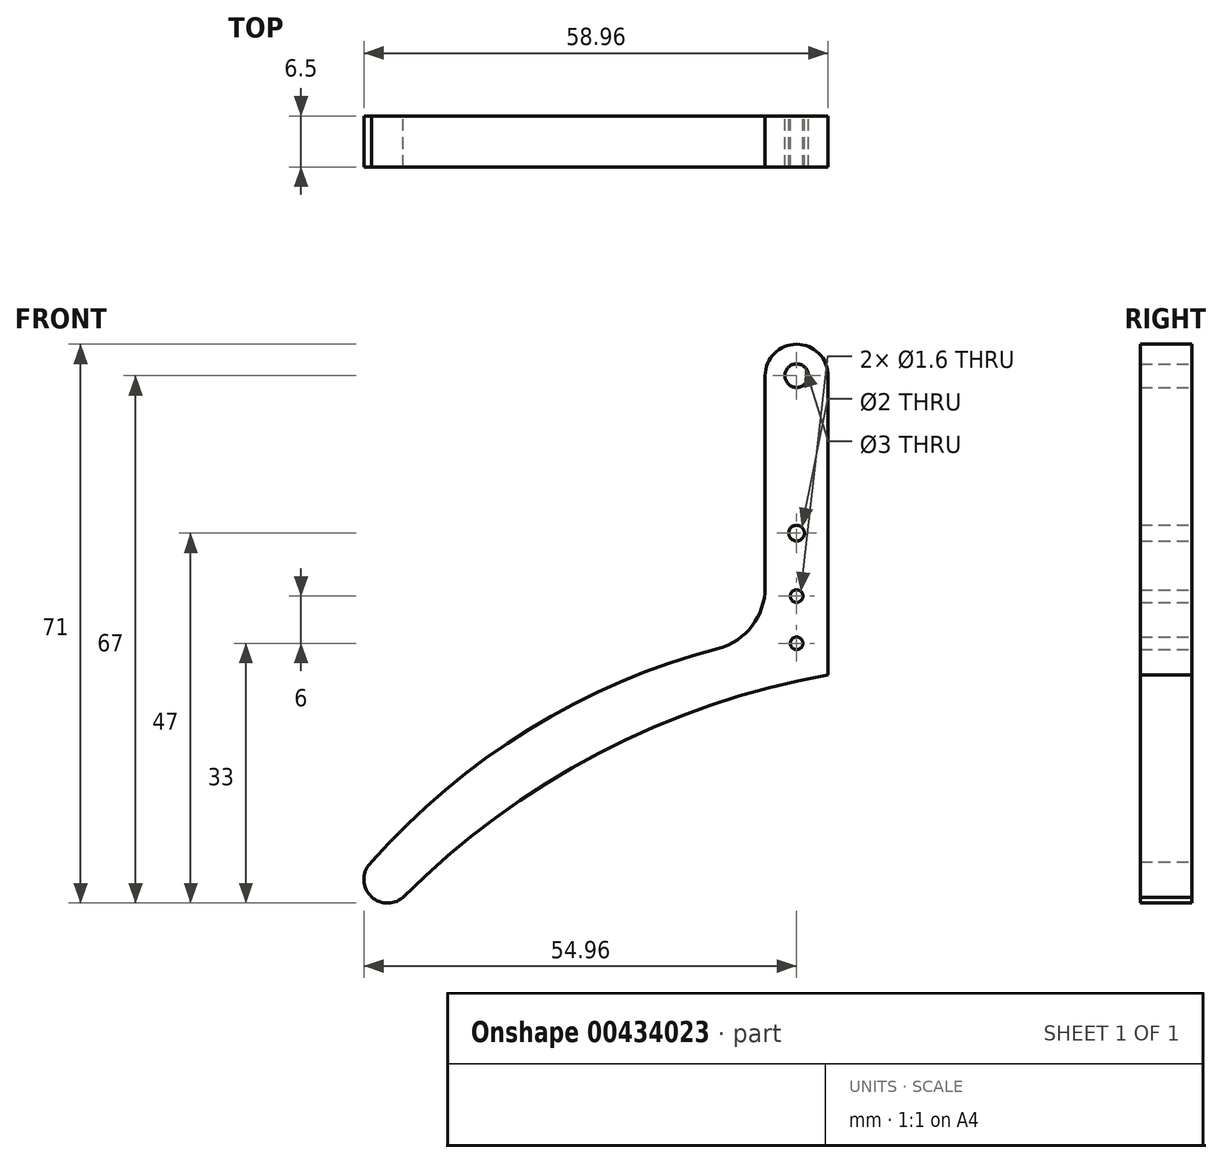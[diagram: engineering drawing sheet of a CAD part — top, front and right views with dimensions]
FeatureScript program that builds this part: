
annotation { "Feature Type Name" : "Feature", "Feature Type Description" : "" }
export const myFeature = defineFeature(function(context is Context, id is Id, definition is map)
    precondition{}
    {
        {
            var Q0;
            Q0=qCreatedBy(makeId("Front.planeOp"),FACE);
            var sketch = newSketch(context, id + "F0", { "sketchPlane" : qUnion([Q0])});
            skCircle(sketch, "E0", {"center": v(0, 34) * mm, "radius": 4 * mm});
            skCircle(sketch, "E1", {"center": v(0, 0) * mm, "radius": 4 * mm});
            skCircle(sketch, "E2", {"center": v(0, 34) * mm, "radius": 1.5 * mm});
            skCircle(sketch, "E3", {"center": v(-51.96, -30) * mm, "radius": 3 * mm});
            skLineSegment(sketch, "E4", {"start": v(-4, 34) * mm, "end": v(-4, 7.1) * mm});
            skLineSegment(sketch, "E5", {"start": v(4, 34) * mm, "end": v(4, 0) * mm});
            skCircle(sketch, "E6", {"center": v(0, 14) * mm, "radius": 1 * mm});
            skLineSegment(sketch, "E7.bottom", {"start": v(4, 0) * mm, "end": v(0, 0) * mm});
            skLineSegment(sketch, "E7.top", {"start": v(4, -4) * mm, "end": v(0, -4) * mm});
            skLineSegment(sketch, "E7.left", {"start": v(4, 0) * mm, "end": v(4, -4) * mm});
            skLineSegment(sketch, "E7.right", {"start": v(0, 0) * mm, "end": v(0, -4) * mm});
            skLineSegment(sketch, "E8.left", {"start": v(0, 0) * mm, "end": v(0, 34) * mm});
            skLineSegment(sketch, "E9", {"start": v(0, 0) * mm, "end": v(-51.96, -30) * mm, "construction": true});
            skPoint(sketch, "E10.visualSharp", {"position": v(-4, 0) * mm});
            skArc(sketch, "E11.filletArc", {"start": v(-9.94, -0.64) * mm, "mid": v(-5.66, 2.22) * mm, "end": v(-4, 7.1) * mm});
            skCircle(sketch, "E12", {"center": v(0, 6) * mm, "radius": 0.8 * mm});
            skCircle(sketch, "E13", {"center": v(0, 0) * mm, "radius": 0.8 * mm});
            skArc(sketch, "E14", {"start": v(-9.94, -0.64) * mm, "mid": v(-33.99, -10.93) * mm, "end": v(-54, -27.8) * mm});
            skArc(sketch, "E15", {"start": v(4, -4) * mm, "mid": v(-25.18, -14) * mm, "end": v(-50.02, -32.28) * mm});
            skSolve(sketch);
        }
        {
            var Q0;
            Q0=makeQuery(id+"F0.imprint","IMPRINT",FACE,{"disambiguationData":[TD([[makeQuery(id+"F0.imprint","IMPRINT",EDGE,{"derivedFrom":sQuery(id+"F0.wireOp",EDGE,"E2")}),-1.0]])]});
            var Q1;
            {var subQ0=sQuery(id+"F0.wireOp",EDGE,"E5");Q1=makeQuery(id+"F0.imprint","IMPRINT",FACE,{"disambiguationData":[TD([[makeQuery(id+"F0.imprint","IMPRINT",EDGE,{"derivedFrom":subQ0}),-1.0]])]});}
            var Q2;
            {var subQ5=sQuery(id+"F0.wireOp",EDGE,"E4");Q2=makeQuery(id+"F0.imprint","IMPRINT",FACE,{"disambiguationData":[TD([[makeQuery(id+"F0.imprint","IMPRINT",EDGE,{"derivedFrom":subQ5}),1.0]])]});}
            var Q3;
            {var subQ0=sQuery(id+"F0.wireOp",EDGE,"E7.bottom");var subQ5=sQuery(id+"F0.wireOp",EDGE,"E13");var subQ6=makeQuery(id+"F0.imprint","INTERSECT",VERTEX,{"derivedFrom":[subQ0,subQ5]});Q3=makeQuery(id+"F0.imprint","IMPRINT",FACE,{"disambiguationData":[TD([[makeQuery(id+"F0.imprint","IMPRINT",EDGE,{"disambiguationData":[TD([[subQ6,1.0]])],"derivedFrom":subQ5}),-1.0]])]});}
            var Q4;
            {var subQ2=sQuery(id+"F0.wireOp",EDGE,"E7.top");Q4=makeQuery(id+"F0.imprint","IMPRINT",FACE,{"disambiguationData":[TD([[makeQuery(id+"F0.imprint","IMPRINT",EDGE,{"derivedFrom":subQ2}),-1.0]])]});}
            var Q5;
            {var subQ1=sQuery(id+"F0.wireOp",EDGE,"E1");var subQ3=sQuery(id+"F0.wireOp",EDGE,"E8.left");var subQ4=makeQuery(id+"F0.imprint","INTERSECT",VERTEX,{"derivedFrom":[subQ1,subQ3]});Q5=makeQuery(id+"F0.imprint","IMPRINT",FACE,{"disambiguationData":[TD([[makeQuery(id+"F0.imprint","IMPRINT",EDGE,{"disambiguationData":[TD([[subQ4,1.0]])],"derivedFrom":subQ3}),1.0]])]});}
            var Q6;
            {var subQ1=sQuery(id+"F0.wireOp",EDGE,"E1");var subQ3=sQuery(id+"F0.wireOp",EDGE,"E8.left");var subQ4=makeQuery(id+"F0.imprint","INTERSECT",VERTEX,{"derivedFrom":[subQ1,subQ3]});Q6=makeQuery(id+"F0.imprint","IMPRINT",FACE,{"disambiguationData":[TD([[makeQuery(id+"F0.imprint","IMPRINT",EDGE,{"disambiguationData":[TD([[subQ4,1.0]])],"derivedFrom":subQ3}),-1.0]])]});}
            var Q7;
            {var subQ0=sQuery(id+"F0.wireOp",EDGE,"E3");var subQ1=makeQuery(id+"F0.imprint","INTERSECT",VERTEX,{"derivedFrom":[subQ0,sQuery(id+"F0.wireOp",EDGE,"E14")]});Q7=makeQuery(id+"F0.imprint","IMPRINT",FACE,{"disambiguationData":[TD([[makeQuery(id+"F0.imprint","IMPRINT",EDGE,{"disambiguationData":[TD([[subQ1,-1.0]])],"derivedFrom":subQ0}),1.0]])]});}
            extrude(context, id + "F1", {"entities" : qUnion([Q0, Q1, Q2, Q3, Q4, Q5, Q6, Q7]), "depth" : 6.5 * mm});
        }
    });
